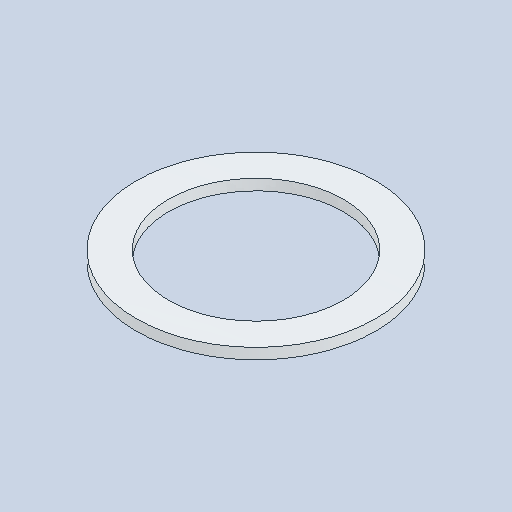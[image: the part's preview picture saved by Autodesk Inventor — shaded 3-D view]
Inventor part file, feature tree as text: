
AUTODESK INVENTOR PART (.ipt)
format: ipt  version: 2024.2 (Build 282272000, 272)  size: 88,064 bytes
history: native  units: in
note: dims shown in document units (in); Inventor stores cm internally (conversion verified against a paired STEP export)
features: revolve x1
ambient origin geometry x8: Origin, YZ Plane, XZ Plane, XY Plane, X Axis, Y Axis, Z Axis, Center Point
bodies: Solid1 (feature_tree)
feature tree (1):
  revolve  "Revolve1"  [1 undecoded]
note: 1 required parameter value undecoded (feature->parameter linkage not recoverable at this tier; creation-order binding heuristic only, values carry confidence <= 0.55)
